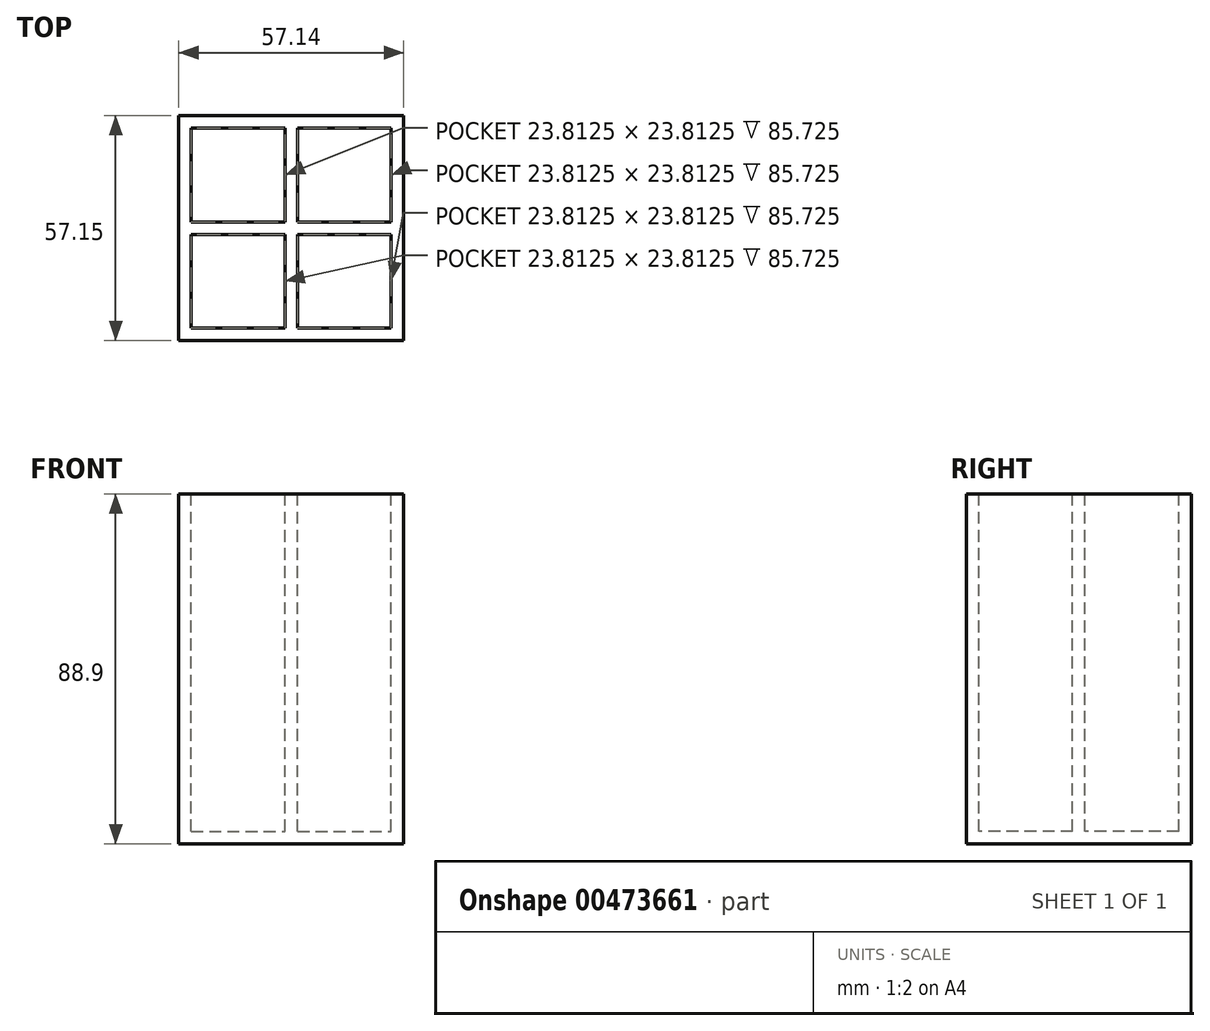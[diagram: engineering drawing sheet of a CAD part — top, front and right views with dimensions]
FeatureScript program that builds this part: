
annotation { "Feature Type Name" : "Feature", "Feature Type Description" : "" }
export const myFeature = defineFeature(function(context is Context, id is Id, definition is map)
    precondition{}
    {
        {
            var Q0;
            Q0=qCreatedBy(makeId("Front.planeOp"),FACE);
            var sketch = newSketch(context, id + "F0", { "sketchPlane" : qUnion([Q0])});
            skLineSegment(sketch, "E0.bottom", {"start": v(28.58, 44.45) * mm, "end": v(-28.58, 44.45) * mm});
            skLineSegment(sketch, "E0.top", {"start": v(28.58, -44.45) * mm, "end": v(-28.57, -44.45) * mm});
            skLineSegment(sketch, "E0.left", {"start": v(28.58, 44.45) * mm, "end": v(28.58, -44.45) * mm});
            skLineSegment(sketch, "E0.right", {"start": v(-28.58, 44.45) * mm, "end": v(-28.58, -44.45) * mm});
            skPoint(sketch, "E0.middle", {"position": v(0, 0) * mm});
            skSolve(sketch);
        }
        {
            var Q0;
            Q0=makeQuery(id+"F0.imprint","IMPRINT",FACE,{"disambiguationData":[TD([[makeQuery(id+"F0.imprint","IMPRINT",EDGE,{"derivedFrom":sQuery(id+"F0.wireOp",EDGE,"E0.bottom")}),1.0]])]});
            extrude(context, id + "F1", {"entities" : qUnion([Q0]), "depth" : 57.15 * mm});
        }
        {
            var Q0;
            Q0=makeQuery(id+"F1.opExtrude","SWEPT_FACE",FACE,{"disambiguationData":[OSD([sQuery(id+"F0.wireOp",EDGE,"E0.bottom")])]});
            var sketch = newSketch(context, id + "F2", { "sketchPlane" : qUnion([Q0])});
            skLineSegment(sketch, "E1.bottom", {"start": v(-25.4, -3.18) * mm, "end": v(-1.59, -3.18) * mm});
            skLineSegment(sketch, "E1.top", {"start": v(-25.4, -26.99) * mm, "end": v(-1.59, -26.99) * mm});
            skLineSegment(sketch, "E1.left", {"start": v(-25.4, -3.18) * mm, "end": v(-25.4, -26.99) * mm});
            skLineSegment(sketch, "E1.right", {"start": v(-1.59, -3.17) * mm, "end": v(-1.59, -26.99) * mm});
            skLineSegment(sketch, "E2.bottom", {"start": v(1.59, -3.18) * mm, "end": v(25.4, -3.18) * mm});
            skLineSegment(sketch, "E2.top", {"start": v(1.59, -26.99) * mm, "end": v(25.4, -26.99) * mm});
            skLineSegment(sketch, "E2.left", {"start": v(1.59, -3.18) * mm, "end": v(1.59, -26.99) * mm});
            skLineSegment(sketch, "E2.right", {"start": v(25.4, -3.17) * mm, "end": v(25.4, -26.99) * mm});
            skLineSegment(sketch, "E3.bottom", {"start": v(-25.4, -30.16) * mm, "end": v(-1.59, -30.16) * mm});
            skLineSegment(sketch, "E3.top", {"start": v(-25.4, -53.98) * mm, "end": v(-1.59, -53.98) * mm});
            skLineSegment(sketch, "E3.left", {"start": v(-25.4, -30.16) * mm, "end": v(-25.4, -53.98) * mm});
            skLineSegment(sketch, "E3.right", {"start": v(-1.59, -30.16) * mm, "end": v(-1.59, -53.98) * mm});
            skLineSegment(sketch, "E4.bottom", {"start": v(1.59, -30.16) * mm, "end": v(25.4, -30.16) * mm});
            skLineSegment(sketch, "E4.top", {"start": v(1.59, -53.98) * mm, "end": v(25.4, -53.98) * mm});
            skLineSegment(sketch, "E4.left", {"start": v(1.59, -30.16) * mm, "end": v(1.59, -53.98) * mm});
            skLineSegment(sketch, "E4.right", {"start": v(25.4, -30.16) * mm, "end": v(25.4, -53.98) * mm});
            skSolve(sketch);
        }
        {
            var Q0;
            Q0=makeQuery(id+"F2.imprint","IMPRINT",FACE,{"disambiguationData":[TD([[makeQuery(id+"F2.imprint","IMPRINT",EDGE,{"derivedFrom":sQuery(id+"F2.wireOp",EDGE,"E1.bottom")}),-1.0]])]});
            var Q1;
            Q1=makeQuery(id+"F2.imprint","IMPRINT",FACE,{"disambiguationData":[TD([[makeQuery(id+"F2.imprint","IMPRINT",EDGE,{"derivedFrom":sQuery(id+"F2.wireOp",EDGE,"E2.bottom")}),-1.0]])]});
            var Q2;
            Q2=makeQuery(id+"F2.imprint","IMPRINT",FACE,{"disambiguationData":[TD([[makeQuery(id+"F2.imprint","IMPRINT",EDGE,{"derivedFrom":sQuery(id+"F2.wireOp",EDGE,"E4.bottom")}),-1.0]])]});
            var Q3;
            Q3=makeQuery(id+"F2.imprint","IMPRINT",FACE,{"disambiguationData":[TD([[makeQuery(id+"F2.imprint","IMPRINT",EDGE,{"derivedFrom":sQuery(id+"F2.wireOp",EDGE,"E3.bottom")}),-1.0]])]});
            extrude(context, id + "F3", {"entities" : qUnion([Q0, Q1, Q2, Q3]), "operationType" : NewBodyOperationType.REMOVE, "oppositeDirection" : true, "depth" : 85.72 * mm});
        }
    });
